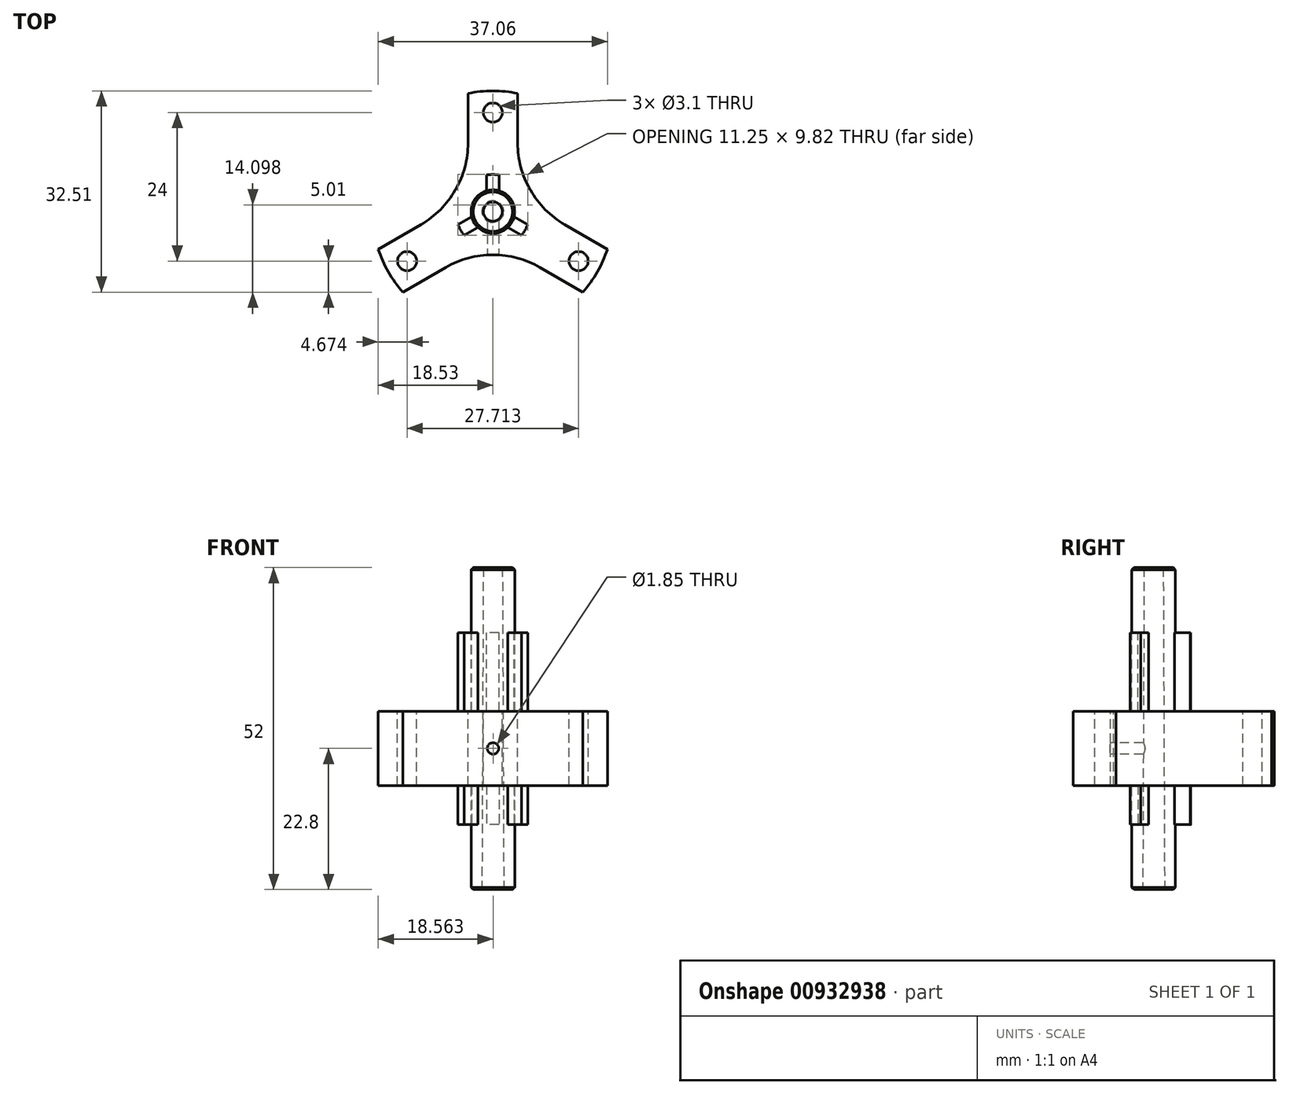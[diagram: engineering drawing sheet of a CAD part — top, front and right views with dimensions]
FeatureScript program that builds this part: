
annotation { "Feature Type Name" : "Feature", "Feature Type Description" : "" }
export const myFeature = defineFeature(function(context is Context, id is Id, definition is map)
    precondition{}
    {
        {
            var Q0;
            Q0=qCreatedBy(makeId("Front.planeOp"),FACE);
            var sketch = newSketch(context, id + "F0", { "sketchPlane" : qUnion([Q0])});
            skLineSegment(sketch, "E0", {"start": v(1.76, 0) * mm, "end": v(3.52, 0) * mm});
            skLineSegment(sketch, "E1", {"start": v(3.52, 0) * mm, "end": v(3.52, 10.5) * mm});
            skLineSegment(sketch, "E2", {"start": v(3.53, 10.5) * mm, "end": v(6, 10.5) * mm});
            skLineSegment(sketch, "E3", {"start": v(6, 10.5) * mm, "end": v(6, 16.8) * mm});
            skLineSegment(sketch, "E4", {"start": v(6, 16.8) * mm, "end": v(19.5, 16.8) * mm});
            skLineSegment(sketch, "E5", {"start": v(19.5, 16.8) * mm, "end": v(19.5, 28.8) * mm});
            skLineSegment(sketch, "E6", {"start": v(19.5, 28.8) * mm, "end": v(6, 28.8) * mm});
            skLineSegment(sketch, "E7", {"start": v(6, 28.8) * mm, "end": v(6, 41.5) * mm});
            skLineSegment(sketch, "E8", {"start": v(6, 41.5) * mm, "end": v(3.52, 41.5) * mm});
            skLineSegment(sketch, "E9", {"start": v(3.52, 41.5) * mm, "end": v(3.52, 52) * mm});
            skLineSegment(sketch, "E10", {"start": v(3.52, 52) * mm, "end": v(1.55, 52) * mm});
            skLineSegment(sketch, "E11", {"start": v(1.76, 0) * mm, "end": v(1.55, 52) * mm});
            skPoint(sketch, "E12.end.orphan", {"position": v(0, 0) * mm});
            skLineSegment(sketch, "E13", {"start": v(0, 51.8) * mm, "end": v(0, -9.02) * mm});
            skSolve(sketch);
        }
        {
            var Q0;
            Q0 = qSketchRegion(id + "F0", true);
            var Q1;
            Q1=sQuery(id+"F0.wireOp",EDGE,"E13");
            revolve(context, id + "F1", {"surfaceOperationType" : NewSurfaceOperationType.NEW, "entities" : qUnion([Q0]), "axis" : qUnion([Q1]), "revolveType" : RevolveType.FULL});
        }
        {
            var Q0;
            Q0=makeQuery(id+"F1.opRevolve","SWEPT_FACE",FACE,{"disambiguationData":[OSD([sQuery(id+"F0.wireOp",EDGE,"E8")])]});
            var sketch = newSketch(context, id + "F2", { "sketchPlane" : qUnion([Q0])});
            skLineSegment(sketch, "E14", {"start": v(-1, 3.38) * mm, "end": v(-1, 5.92) * mm});
            skLineSegment(sketch, "E15", {"start": v(1, 5.92) * mm, "end": v(1, 3.38) * mm});
            skArc(sketch, "E16", {"start": v(-1, 5.92) * mm, "mid": v(0, 6) * mm, "end": v(1, 5.92) * mm});
            skArc(sketch, "E17", {"start": v(-1, 3.38) * mm, "mid": v(0, 3.52) * mm, "end": v(1, 3.38) * mm});
            skLineSegment(sketch, "E18", {"start": v(0, 6.9) * mm, "end": v(0, 2.48) * mm, "construction": true});
            skPoint(sketch, "E18.startSnap0", {"position": v(0, 6) * mm});
            skLineSegment(sketch, "E19.1.0", {"start": v(-2.43, -2.56) * mm, "end": v(-4.62, -3.82) * mm});
            skArc(sketch, "E19.1.1", {"start": v(-2.43, -2.56) * mm, "mid": v(-3.05, -1.76) * mm, "end": v(-3.43, -0.82) * mm});
            skLineSegment(sketch, "E19.1.2", {"start": v(-5.62, -2.1) * mm, "end": v(-3.43, -0.82) * mm});
            skArc(sketch, "E19.1.3", {"start": v(-4.62, -3.82) * mm, "mid": v(-5.2, -3) * mm, "end": v(-5.62, -2.1) * mm});
            skLineSegment(sketch, "E19.2.0", {"start": v(3.43, -0.82) * mm, "end": v(5.62, -2.1) * mm});
            skArc(sketch, "E19.2.1", {"start": v(3.43, -0.82) * mm, "mid": v(3.05, -1.76) * mm, "end": v(2.43, -2.56) * mm});
            skLineSegment(sketch, "E19.2.2", {"start": v(4.62, -3.82) * mm, "end": v(2.43, -2.56) * mm});
            skArc(sketch, "E19.2.3", {"start": v(5.62, -2.1) * mm, "mid": v(5.2, -3) * mm, "end": v(4.62, -3.82) * mm});
            skSolve(sketch);
        }
        {
            var Q0;
            {var subQ0=sQuery(id+"F2.wireOp",EDGE,"E14");Q0=makeQuery(id+"F2.imprint","IMPRINT",FACE,{"disambiguationData":[TD([[makeQuery(id+"F2.imprint","IMPRINT",EDGE,{"derivedFrom":subQ0}),1.0]])]});}
            var Q1;
            {var subQ0=sQuery(id+"F2.wireOp",EDGE,"E15");Q1=makeQuery(id+"F2.imprint","IMPRINT",FACE,{"disambiguationData":[TD([[makeQuery(id+"F2.imprint","IMPRINT",EDGE,{"derivedFrom":subQ0}),1.0]])]});}
            var Q2;
            {var subQ0=sQuery(id+"F2.wireOp",EDGE,"E19.1.0");Q2=makeQuery(id+"F2.imprint","IMPRINT",FACE,{"disambiguationData":[TD([[makeQuery(id+"F2.imprint","IMPRINT",EDGE,{"derivedFrom":subQ0}),1.0]])]});}
            var Q3;
            Q3=makeQuery(id+"F1.opRevolve","SWEPT_FACE",FACE,{"disambiguationData":[OSD([sQuery(id+"F0.wireOp",EDGE,"E6")])]});
            extrude(context, id + "F3", {"entities" : qUnion([Q0, Q1, Q2]), "operationType" : NewBodyOperationType.REMOVE, "endBound" : BoundingType.UP_TO_SURFACE, "oppositeDirection" : true, "depth" : 25 * mm, "endBoundEntityFace" : qUnion([Q3]), "offsetDistance" : 25 * mm});
        }
        {
            var Q0;
            Q0=makeQuery(id+"F1.opRevolve","SWEPT_FACE",FACE,{"disambiguationData":[OSD([sQuery(id+"F0.wireOp",EDGE,"E2")])]});
            var sketch = newSketch(context, id + "F4", { "sketchPlane" : qUnion([Q0])});
            skPoint(sketch, "E20.center", {"position": v(0, 0) * mm});
            skArc(sketch, "E21.0", {"start": v(-4.62, 3.82) * mm, "mid": v(-5.2, 3) * mm, "end": v(-5.62, 2.1) * mm});
            skLineSegment(sketch, "E22.0", {"start": v(-2.43, 2.56) * mm, "end": v(-4.62, 3.82) * mm});
            skLineSegment(sketch, "E23.0", {"start": v(-5.62, 2.1) * mm, "end": v(-3.43, 0.82) * mm});
            skArc(sketch, "E24.0", {"start": v(-2.43, 2.56) * mm, "mid": v(-3.05, 1.76) * mm, "end": v(-3.43, 0.82) * mm});
            skLineSegment(sketch, "E25.0", {"start": v(4.62, 3.82) * mm, "end": v(2.43, 2.56) * mm});
            skArc(sketch, "E26.0", {"start": v(3.43, 0.82) * mm, "mid": v(3.05, 1.76) * mm, "end": v(2.43, 2.56) * mm});
            skLineSegment(sketch, "E27.0", {"start": v(3.43, 0.82) * mm, "end": v(5.62, 2.1) * mm});
            skArc(sketch, "E28.0", {"start": v(5.62, 2.1) * mm, "mid": v(5.2, 3) * mm, "end": v(4.62, 3.82) * mm});
            skArc(sketch, "E29.0", {"start": v(-1, -3.38) * mm, "mid": v(0, -3.52) * mm, "end": v(1, -3.38) * mm});
            skLineSegment(sketch, "E30.0", {"start": v(-1, -3.38) * mm, "end": v(-1, -5.92) * mm});
            skLineSegment(sketch, "E31.0", {"start": v(1, -5.92) * mm, "end": v(1, -3.38) * mm});
            skArc(sketch, "E32.0", {"start": v(-1, -5.92) * mm, "mid": v(0, -6) * mm, "end": v(1, -5.92) * mm});
            skSolve(sketch);
        }
        {
            var Q0;
            {var subQ0=sQuery(id+"F4.wireOp",EDGE,"E22.0");Q0=makeQuery(id+"F4.imprint","IMPRINT",FACE,{"disambiguationData":[TD([[makeQuery(id+"F4.imprint","IMPRINT",EDGE,{"derivedFrom":subQ0}),-1.0]])]});}
            var Q1;
            {var subQ0=sQuery(id+"F4.wireOp",EDGE,"E23.0");Q1=makeQuery(id+"F4.imprint","IMPRINT",FACE,{"disambiguationData":[TD([[makeQuery(id+"F4.imprint","IMPRINT",EDGE,{"derivedFrom":subQ0}),-1.0]])]});}
            var Q2;
            {var subQ0=sQuery(id+"F4.wireOp",EDGE,"E27.0");Q2=makeQuery(id+"F4.imprint","IMPRINT",FACE,{"disambiguationData":[TD([[makeQuery(id+"F4.imprint","IMPRINT",EDGE,{"derivedFrom":subQ0}),-1.0]])]});}
            var Q3;
            Q3=makeQuery(id+"F1.opRevolve","SWEPT_FACE",FACE,{"disambiguationData":[OSD([sQuery(id+"F0.wireOp",EDGE,"E4")])]});
            extrude(context, id + "F5", {"entities" : qUnion([Q0, Q1, Q2]), "operationType" : NewBodyOperationType.REMOVE, "endBound" : BoundingType.UP_TO_SURFACE, "oppositeDirection" : true, "depth" : 25 * mm, "endBoundEntityFace" : qUnion([Q3]), "offsetDistance" : 25 * mm});
        }
        {
            var Q0;
            Q0=makeQuery(id+"F1.opRevolve","SWEPT_FACE",FACE,{"disambiguationData":[OSD([sQuery(id+"F0.wireOp",EDGE,"E6")])]});
            var sketch = newSketch(context, id + "F6", { "sketchPlane" : qUnion([Q0])});
            skCircle(sketch, "E33", {"center": v(0, 16) * mm, "radius": 1.55 * mm});
            skPoint(sketch, "E34.center", {"position": v(0, 0) * mm});
            skCircle(sketch, "E35", {"center": v(0, 0) * mm, "radius": 7 * mm});
            skCircle(sketch, "E36", {"center": v(0, 16) * mm, "radius": 2.75 * mm, "construction": true});
            skLineSegment(sketch, "E37", {"start": v(4, 5.74) * mm, "end": v(4, 19.09) * mm});
            skLineSegment(sketch, "E38", {"start": v(-4, 5.74) * mm, "end": v(-4, 19.09) * mm});
            skArc(sketch, "E39", {"start": v(-4, 19.09) * mm, "mid": v(0, 19.5) * mm, "end": v(4, 19.09) * mm});
            skLineSegment(sketch, "E40.1.0", {"start": v(-2.97, -6.34) * mm, "end": v(-14.53, -13) * mm});
            skLineSegment(sketch, "E40.1.1", {"start": v(-6.97, 0.6) * mm, "end": v(-18.53, -6.08) * mm});
            skArc(sketch, "E40.1.2", {"start": v(-14.53, -13) * mm, "mid": v(-16.89, -9.75) * mm, "end": v(-18.53, -6.08) * mm});
            skCircle(sketch, "E40.1.3", {"center": v(-13.86, -8) * mm, "radius": 1.55 * mm});
            skLineSegment(sketch, "E40.2.0", {"start": v(6.97, 0.6) * mm, "end": v(18.53, -6.08) * mm});
            skLineSegment(sketch, "E40.2.1", {"start": v(2.97, -6.34) * mm, "end": v(14.53, -13) * mm});
            skArc(sketch, "E40.2.2", {"start": v(18.53, -6.08) * mm, "mid": v(16.89, -9.75) * mm, "end": v(14.53, -13) * mm});
            skCircle(sketch, "E40.2.3", {"center": v(13.86, -8) * mm, "radius": 1.55 * mm});
            skSolve(sketch);
        }
        {
            var Q0;
            Q0=makeQuery(id+"F6.imprint","IMPRINT",FACE,{"disambiguationData":[TD([[makeQuery(id+"F6.imprint","IMPRINT",EDGE,{"derivedFrom":sQuery(id+"F6.wireOp",EDGE,"E33")}),1.0]])]});
            var Q1;
            {var subQ0=sQuery(id+"F6.wireOp",EDGE,"E38");Q1=makeQuery(id+"F6.imprint","IMPRINT",FACE,{"disambiguationData":[TD([[makeQuery(id+"F6.imprint","IMPRINT",EDGE,{"derivedFrom":subQ0}),1.0]])]});}
            var Q2;
            {var subQ0=sQuery(id+"F6.wireOp",EDGE,"E37");Q2=makeQuery(id+"F6.imprint","IMPRINT",FACE,{"disambiguationData":[TD([[makeQuery(id+"F6.imprint","IMPRINT",EDGE,{"derivedFrom":subQ0}),-1.0]])]});}
            var Q3;
            Q3=makeQuery(id+"F6.imprint","IMPRINT",FACE,{"disambiguationData":[TD([[makeQuery(id+"F6.imprint","IMPRINT",EDGE,{"derivedFrom":sQuery(id+"F6.wireOp",EDGE,"E40.2.3")}),1.0]])]});
            var Q4;
            {var subQ0=sQuery(id+"F6.wireOp",EDGE,"E40.1.0");Q4=makeQuery(id+"F6.imprint","IMPRINT",FACE,{"disambiguationData":[TD([[makeQuery(id+"F6.imprint","IMPRINT",EDGE,{"derivedFrom":subQ0}),1.0]])]});}
            var Q5;
            Q5=makeQuery(id+"F6.imprint","IMPRINT",FACE,{"disambiguationData":[TD([[makeQuery(id+"F6.imprint","IMPRINT",EDGE,{"derivedFrom":sQuery(id+"F6.wireOp",EDGE,"E40.1.3")}),1.0]])]});
            extrude(context, id + "F7", {"entities" : qUnion([Q0, Q1, Q2, Q3, Q4, Q5]), "operationType" : NewBodyOperationType.REMOVE, "endBound" : BoundingType.THROUGH_ALL, "oppositeDirection" : true, "depth" : 25 * mm, "offsetDistance" : 25 * mm});
        }
        {
            var Q0;
            Q0=makeQuery(id+"F7.boolean.opBoolean","COPY",EDGE,{"derivedFrom":makeQuery(id+"F7.opExtrude","SWEPT_EDGE",EDGE,{"disambiguationData":[OSD([sQuery(id+"F6.wireOp",EDGE,"E35"),sQuery(id+"F6.wireOp",EDGE,"ddfacb70-5919-4228-9e49-a10853ac0f06.2.2")])]})});
            var Q1;
            Q1=makeQuery(id+"F7.boolean.opBoolean","COPY",EDGE,{"derivedFrom":makeQuery(id+"F7.opExtrude","SWEPT_EDGE",EDGE,{"disambiguationData":[OSD([sQuery(id+"F6.wireOp",EDGE,"E35"),sQuery(id+"F6.wireOp",EDGE,"ddfacb70-5919-4228-9e49-a10853ac0f06.1.0")])]})});
            var Q2;
            Q2=makeQuery(id+"F7.boolean.opBoolean","COPY",EDGE,{"derivedFrom":makeQuery(id+"F7.opExtrude","SWEPT_EDGE",EDGE,{"disambiguationData":[OSD([sQuery(id+"F6.wireOp",EDGE,"E35"),sQuery(id+"F6.wireOp",EDGE,"ddfacb70-5919-4228-9e49-a10853ac0f06.1.2")])]})});
            var Q3;
            Q3=makeQuery(id+"F7.boolean.opBoolean","COPY",EDGE,{"derivedFrom":makeQuery(id+"F7.opExtrude","SWEPT_EDGE",EDGE,{"disambiguationData":[OSD([sQuery(id+"F6.wireOp",EDGE,"E35"),sQuery(id+"F6.wireOp",EDGE,"E38")])]})});
            var Q4;
            Q4=makeQuery(id+"F7.boolean.opBoolean","COPY",EDGE,{"derivedFrom":makeQuery(id+"F7.opExtrude","SWEPT_EDGE",EDGE,{"disambiguationData":[OSD([sQuery(id+"F6.wireOp",EDGE,"E35"),sQuery(id+"F6.wireOp",EDGE,"ddfacb70-5919-4228-9e49-a10853ac0f06.2.0")])]})});
            var Q5;
            Q5=makeQuery(id+"F7.boolean.opBoolean","COPY",EDGE,{"derivedFrom":makeQuery(id+"F7.opExtrude","SWEPT_EDGE",EDGE,{"disambiguationData":[OSD([sQuery(id+"F6.wireOp",EDGE,"E35"),sQuery(id+"F6.wireOp",EDGE,"E37")])]})});
            fillet(context, id + "F8", {"entities" : qUnion([Q0, Q1, Q2, Q3, Q4, Q5]), "radius" : 15 * mm, "tangentPropagation" : true, "allowEdgeOverflow" : false});
        }
        {
            var Q0;
            Q0=qCreatedBy(makeId("Front.planeOp"),FACE);
            cPlane(context, id + "F9", {"entities" : qUnion([Q0]), "cplaneType" : CPlaneType.OFFSET, "offset" : 7.5 * mm, "width" : 150 * mm, "height" : 150 * mm});
        }
        {
            var Q0;
            Q0=qCreatedBy(id+"F9.planeOp",FACE);
            var sketch = newSketch(context, id + "F10", { "sketchPlane" : qUnion([Q0])});
            skPoint(sketch, "E41.0", {"position": v(0.03, 22.8) * mm});
            skCircle(sketch, "E42", {"center": v(0.03, 22.8) * mm, "radius": 0.93 * mm});
            skSolve(sketch);
        }
        {
            var Q0;
            Q0=makeQuery(id+"F10.imprint","IMPRINT",FACE,{"disambiguationData":[TD([[makeQuery(id+"F10.imprint","IMPRINT",EDGE,{"derivedFrom":sQuery(id+"F10.wireOp",EDGE,"E42")}),1.0]])]});
            var Q1;
            Q1=makeQuery(id+"F1.opRevolve","SWEPT_FACE",FACE,{"disambiguationData":[OSD([sQuery(id+"F0.wireOp",EDGE,"E11")])]});
            extrude(context, id + "F11", {"entities" : qUnion([Q0]), "operationType" : NewBodyOperationType.REMOVE, "endBound" : BoundingType.UP_TO_SURFACE, "oppositeDirection" : true, "depth" : 25 * mm, "endBoundEntityFace" : qUnion([Q1]), "offsetDistance" : 25 * mm});
        }
        {
            var Q0;
            Q0=makeQuery(id+"F1.opRevolve","SWEPT_EDGE",EDGE,{"disambiguationData":[OSD([sQuery(id+"F0.wireOp",EDGE,"E9"),sQuery(id+"F0.wireOp",EDGE,"E10")])]});
            var Q1;
            Q1=makeQuery(id+"F1.opRevolve","SWEPT_EDGE",EDGE,{"disambiguationData":[OSD([sQuery(id+"F0.wireOp",EDGE,"E0"),sQuery(id+"F0.wireOp",EDGE,"E1")])]});
            chamfer(context, id + "F12", {"entities" : qUnion([Q0, Q1]), "width" : 0.35 * mm, "tangentPropagation" : true});
        }
    });
